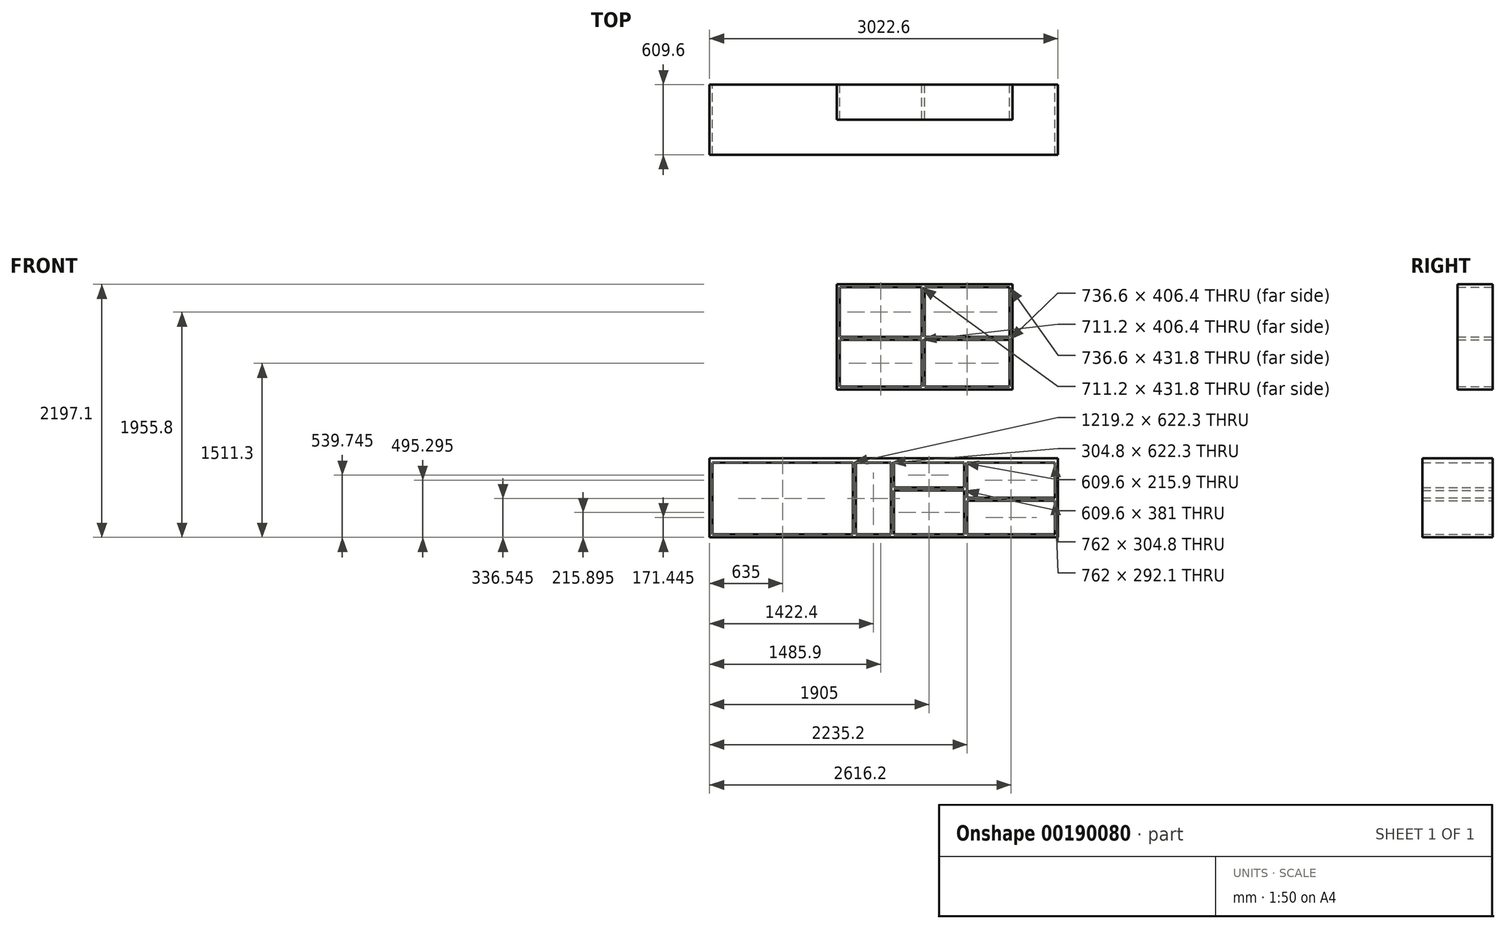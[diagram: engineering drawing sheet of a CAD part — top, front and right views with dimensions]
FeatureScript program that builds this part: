
annotation { "Feature Type Name" : "Feature", "Feature Type Description" : "" }
export const myFeature = defineFeature(function(context is Context, id is Id, definition is map)
    precondition{}
    {
        {
            var Q0;
            Q0=qCreatedBy(makeId("Front.planeOp"),FACE);
            var sketch = newSketch(context, id + "F0", { "sketchPlane" : qUnion([Q0])});
            skLineSegment(sketch, "E0.bottom", {"start": v(1816.1, -1569.73) * mm, "end": v(-1841.5, -1569.73) * mm});
            skLineSegment(sketch, "E0.top", {"start": v(1816.1, 1173.47) * mm, "end": v(-1841.5, 1173.47) * mm});
            skLineSegment(sketch, "E0.left", {"start": v(1816.1, -1569.73) * mm, "end": v(1816.1, 1173.47) * mm});
            skLineSegment(sketch, "E0.right", {"start": v(-1841.5, -1569.73) * mm, "end": v(-1841.5, 1173.47) * mm});
            skLineSegment(sketch, "E1.bottom", {"start": v(-1841.5, -782.33) * mm, "end": v(1181.1, -782.33) * mm});
            skLineSegment(sketch, "E1.top", {"start": v(-1841.5, -1468.13) * mm, "end": v(1816.1, -1468.13) * mm});
            skLineSegment(sketch, "E1.left", {"start": v(-1841.5, -782.33) * mm, "end": v(-1841.5, -1468.13) * mm});
            skLineSegment(sketch, "E2", {"start": v(-1841.5, 1173.47) * mm, "end": v(-1841.5, -1569.73) * mm});
            skLineSegment(sketch, "E3", {"start": v(-1841.5, -1569.73) * mm, "end": v(1816.1, -1569.73) * mm});
            skLineSegment(sketch, "E4.left", {"start": v(-1841.5, -782.33) * mm, "end": v(-1841.5, -185.43) * mm});
            skLineSegment(sketch, "E5.bottom", {"start": v(-736.6, 728.97) * mm, "end": v(787.4, 728.97) * mm});
            skLineSegment(sketch, "E5.top", {"start": v(-736.6, -185.43) * mm, "end": v(787.4, -185.43) * mm});
            skLineSegment(sketch, "E5.left", {"start": v(-736.6, 728.97) * mm, "end": v(-736.6, -185.43) * mm});
            skLineSegment(sketch, "E5.right", {"start": v(787.4, 728.97) * mm, "end": v(787.4, -185.43) * mm});
            skLineSegment(sketch, "E6.bottom", {"start": v(-711.2, 703.57) * mm, "end": v(0, 703.57) * mm});
            skLineSegment(sketch, "E6.top", {"start": v(-711.2, 271.77) * mm, "end": v(0, 271.77) * mm});
            skLineSegment(sketch, "E6.left", {"start": v(-711.2, 703.57) * mm, "end": v(-711.2, 271.77) * mm});
            skLineSegment(sketch, "E6.right", {"start": v(0, 703.57) * mm, "end": v(0, 271.77) * mm});
            skLineSegment(sketch, "E7.bottom", {"start": v(25.4, 703.57) * mm, "end": v(762, 703.57) * mm});
            skLineSegment(sketch, "E7.top", {"start": v(25.4, 271.77) * mm, "end": v(762, 271.77) * mm});
            skLineSegment(sketch, "E7.left", {"start": v(25.4, 703.57) * mm, "end": v(25.4, 271.77) * mm});
            skLineSegment(sketch, "E7.right", {"start": v(762, 703.57) * mm, "end": v(762, 271.77) * mm});
            skLineSegment(sketch, "E8.bottom", {"start": v(-711.2, 246.37) * mm, "end": v(0, 246.37) * mm});
            skLineSegment(sketch, "E8.top", {"start": v(-711.2, -160.03) * mm, "end": v(0, -160.03) * mm});
            skLineSegment(sketch, "E8.left", {"start": v(-711.2, 246.37) * mm, "end": v(-711.2, -160.03) * mm});
            skLineSegment(sketch, "E8.right", {"start": v(0, 246.37) * mm, "end": v(0, -160.03) * mm});
            skLineSegment(sketch, "E9.bottom", {"start": v(25.4, 246.37) * mm, "end": v(762, 246.37) * mm});
            skLineSegment(sketch, "E9.top", {"start": v(25.4, -160.03) * mm, "end": v(762, -160.03) * mm});
            skLineSegment(sketch, "E9.left", {"start": v(25.4, 246.37) * mm, "end": v(25.4, -160.03) * mm});
            skLineSegment(sketch, "E9.right", {"start": v(762, 246.37) * mm, "end": v(762, -160.03) * mm});
            skLineSegment(sketch, "E10.bottom", {"start": v(-1816.1, -820.43) * mm, "end": v(-596.9, -820.43) * mm});
            skLineSegment(sketch, "E10.top", {"start": v(-1816.1, -1442.73) * mm, "end": v(-596.9, -1442.73) * mm});
            skLineSegment(sketch, "E10.left", {"start": v(-1816.1, -820.43) * mm, "end": v(-1816.1, -1442.73) * mm});
            skLineSegment(sketch, "E10.right", {"start": v(-596.9, -820.43) * mm, "end": v(-596.9, -1442.73) * mm});
            skLineSegment(sketch, "E11.bottom", {"start": v(-571.5, -820.43) * mm, "end": v(-266.7, -820.43) * mm});
            skLineSegment(sketch, "E11.top", {"start": v(-571.5, -1442.73) * mm, "end": v(-266.7, -1442.73) * mm});
            skLineSegment(sketch, "E11.left", {"start": v(-571.5, -820.43) * mm, "end": v(-571.5, -1442.73) * mm});
            skLineSegment(sketch, "E11.right", {"start": v(-266.7, -820.43) * mm, "end": v(-266.7, -1442.73) * mm});
            skLineSegment(sketch, "E12.bottom", {"start": v(-241.3, -820.43) * mm, "end": v(368.3, -820.43) * mm});
            skLineSegment(sketch, "E12.top", {"start": v(-241.3, -1036.33) * mm, "end": v(368.3, -1036.33) * mm});
            skLineSegment(sketch, "E12.left", {"start": v(-241.3, -820.43) * mm, "end": v(-241.3, -1036.33) * mm});
            skLineSegment(sketch, "E12.right", {"start": v(368.3, -820.43) * mm, "end": v(368.3, -1036.33) * mm});
            skLineSegment(sketch, "E13.bottom", {"start": v(-241.3, -1061.73) * mm, "end": v(368.3, -1061.73) * mm});
            skLineSegment(sketch, "E13.top", {"start": v(-241.3, -1442.73) * mm, "end": v(368.3, -1442.73) * mm});
            skLineSegment(sketch, "E13.left", {"start": v(-241.3, -1061.73) * mm, "end": v(-241.3, -1442.73) * mm});
            skLineSegment(sketch, "E13.right", {"start": v(368.3, -1061.73) * mm, "end": v(368.3, -1442.73) * mm});
            skLineSegment(sketch, "E14.bottom", {"start": v(393.7, -820.43) * mm, "end": v(1155.7, -820.43) * mm});
            skLineSegment(sketch, "E14.top", {"start": v(393.7, -1125.23) * mm, "end": v(1155.7, -1125.23) * mm});
            skLineSegment(sketch, "E14.left", {"start": v(393.7, -820.43) * mm, "end": v(393.7, -1125.23) * mm});
            skLineSegment(sketch, "E14.right", {"start": v(1155.7, -820.43) * mm, "end": v(1155.7, -1125.23) * mm});
            skLineSegment(sketch, "E15.bottom", {"start": v(393.7, -1150.63) * mm, "end": v(1155.7, -1150.63) * mm});
            skLineSegment(sketch, "E15.top", {"start": v(393.7, -1442.73) * mm, "end": v(1155.7, -1442.73) * mm});
            skLineSegment(sketch, "E15.left", {"start": v(393.7, -1150.63) * mm, "end": v(393.7, -1442.73) * mm});
            skLineSegment(sketch, "E15.right", {"start": v(1155.7, -1150.63) * mm, "end": v(1155.7, -1442.73) * mm});
            skLineSegment(sketch, "E16", {"start": v(1181.1, -782.33) * mm, "end": v(1181.1, -1468.13) * mm});
            skSolve(sketch);
        }
        {
            var Q0;
            Q0=sQuery(id+"F0.wireOp",EDGE,"E2");
            var Q1;
            Q1=sQuery(id+"F0.wireOp",EDGE,"E3");
            extrude(context, id + "F1", {"bodyType" : ToolBodyType.SURFACE, "surfaceEntities" : qUnion([Q0, Q1]), "depth" : 1524 * mm});
        }
        {
            var Q0;
            Q0=makeQuery(id+"F0.imprint","IMPRINT",FACE,{"disambiguationData":[TD([[makeQuery(id+"F0.imprint","IMPRINT",EDGE,{"derivedFrom":sQuery(id+"F0.wireOp",EDGE,"E5.bottom")}),-1.0]])]});
            extrude(context, id + "F2", {"entities" : qUnion([Q0]), "depth" : 304.8 * mm});
        }
        {
            var Q0;
            {var subQ4=sQuery(id+"F0.wireOp",EDGE,"E1.bottom");Q0=makeQuery(id+"F0.imprint","IMPRINT",FACE,{"disambiguationData":[TD([[makeQuery(id+"F0.imprint","IMPRINT",EDGE,{"derivedFrom":subQ4}),-1.0]])]});}
            extrude(context, id + "F3", {"entities" : qUnion([Q0]), "depth" : 609.6 * mm});
        }
    });
